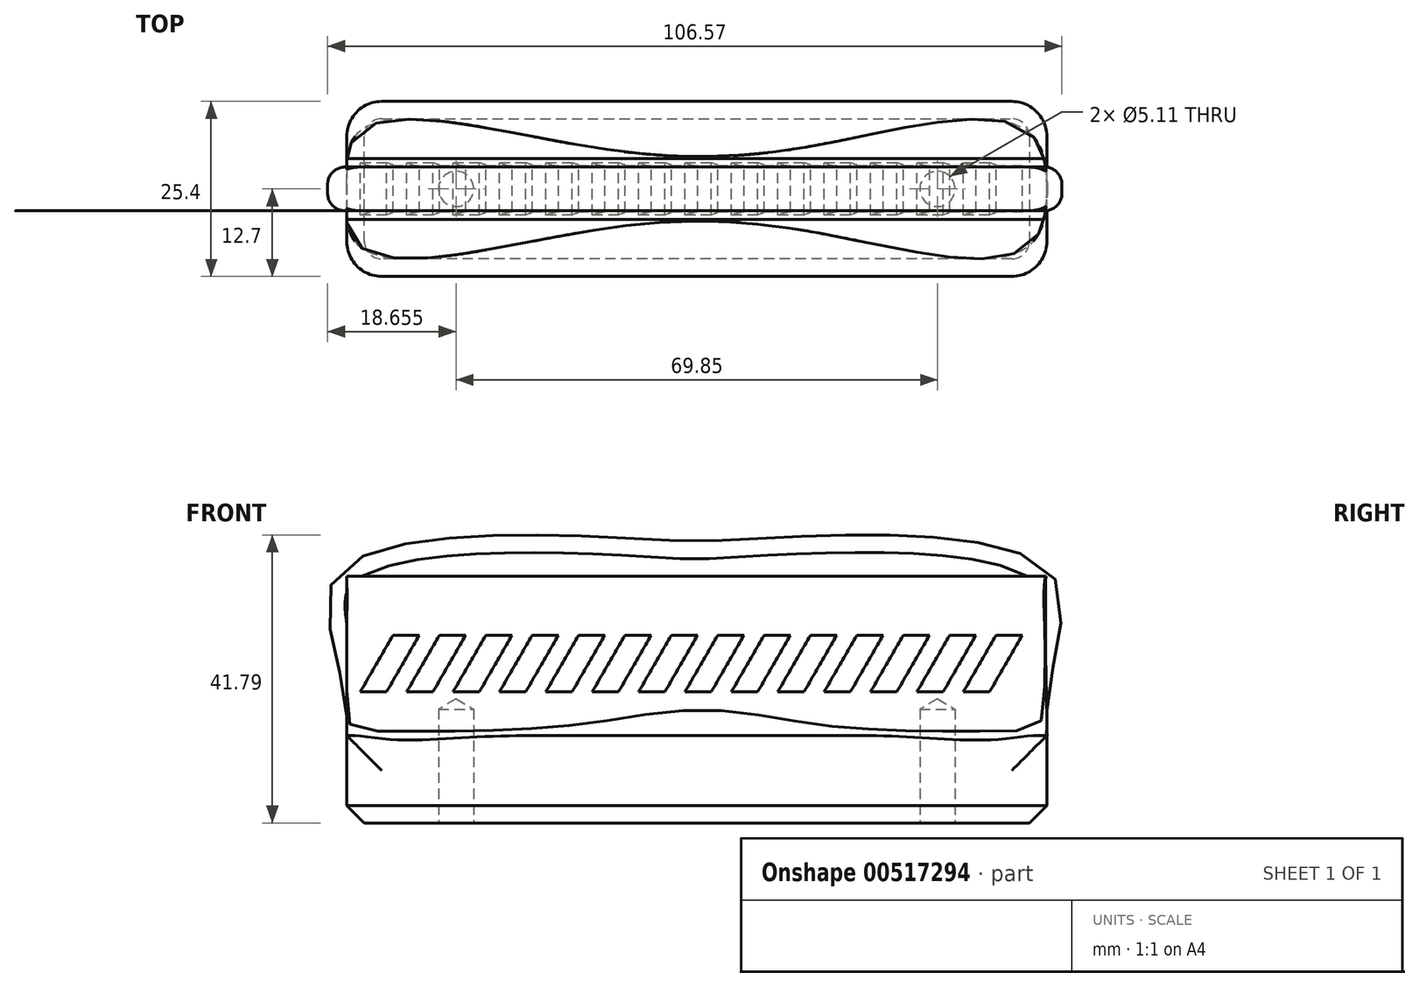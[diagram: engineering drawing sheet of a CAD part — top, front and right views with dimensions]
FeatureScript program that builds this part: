
annotation { "Feature Type Name" : "Feature", "Feature Type Description" : "" }
export const myFeature = defineFeature(function(context is Context, id is Id, definition is map)
    precondition{}
    {
        {
            var Q0;
            Q0=qCreatedBy(makeId("Front.planeOp"),FACE);
            var sketch = newSketch(context, id + "F0", { "sketchPlane" : qUnion([Q0])});
            skLineSegment(sketch, "E0.bottom", {"start": v(50.8, 6.35) * mm, "end": v(-50.8, 6.35) * mm});
            skLineSegment(sketch, "E0.top", {"start": v(50.8, -6.35) * mm, "end": v(-50.8, -6.35) * mm});
            skLineSegment(sketch, "E0.left", {"start": v(50.8, 6.35) * mm, "end": v(50.8, -6.35) * mm});
            skLineSegment(sketch, "E0.right", {"start": v(-50.8, 6.35) * mm, "end": v(-50.8, -6.35) * mm});
            skPoint(sketch, "E0.middle", {"position": v(0, 0) * mm});
            skSolve(sketch);
        }
        {
            var Q0;
            Q0=makeQuery(id+"F0.imprint","IMPRINT",FACE,{"disambiguationData":[TD([[makeQuery(id+"F0.imprint","IMPRINT",EDGE,{"derivedFrom":sQuery(id+"F0.wireOp",EDGE,"E0.bottom")}),1.0]])]});
            extrude(context, id + "F1", {"entities" : qUnion([Q0]), "endBound" : BoundingType.SYMMETRIC, "depth" : 25.4 * mm, "offsetDistance" : 25.4 * mm});
        }
        {
            var Q0;
            Q0=qCreatedBy(makeId("Front.planeOp"),FACE);
            var sketch = newSketch(context, id + "F2", { "sketchPlane" : qUnion([Q0])});
            skFitSpline(sketch, "E1", {"points": [v(-50.78, 6.4) * mm, v(-51.66, 30.38) * mm, v(-5.27, 34.72) * mm, v(5.16, 34.72) * mm, v(50.96, 30.38) * mm, v(50.85, 6.4) * mm], "startDerivative": vector(8.85, 159.27) * mm, "endDerivative": vector(16.11, -153.94) * mm});
            skLineSegment(sketch, "E2", {"start": v(-50.78, 6.4) * mm, "end": v(50.85, 6.4) * mm});
            skSolve(sketch);
        }
        {
            var Q0;
            Q0=makeQuery(id+"F2.imprint","IMPRINT",FACE,{"disambiguationData":[TD([[makeQuery(id+"F2.imprint","IMPRINT",EDGE,{"derivedFrom":sQuery(id+"F2.wireOp",EDGE,"E1")}),-1.0]])]});
            extrude(context, id + "F3", {"entities" : qUnion([Q0]), "operationType" : NewBodyOperationType.ADD, "endBound" : BoundingType.SYMMETRIC, "depth" : 6.35 * mm, "offsetDistance" : 25.4 * mm});
        }
        {
            var Q0;
            Q0=makeQuery(id+"F1.opExtrude","CAP_EDGE",EDGE,{"disambiguationData":[OSD([sQuery(id+"F0.wireOp",EDGE,"E0.right")])],"isStart":false});
            var Q1;
            Q1=makeQuery(id+"F1.opExtrude","CAP_EDGE",EDGE,{"disambiguationData":[OSD([sQuery(id+"F0.wireOp",EDGE,"E0.right")])],"isStart":true});
            var Q2;
            Q2=makeQuery(id+"F1.opExtrude","CAP_EDGE",EDGE,{"disambiguationData":[OSD([sQuery(id+"F0.wireOp",EDGE,"E0.left")])],"isStart":false});
            var Q3;
            Q3=makeQuery(id+"F1.opExtrude","CAP_EDGE",EDGE,{"disambiguationData":[OSD([sQuery(id+"F0.wireOp",EDGE,"E0.left")])],"isStart":true});
            fillet(context, id + "F4", {"entities" : qUnion([Q0, Q1, Q2, Q3]), "radius" : 5.08 * mm, "tangentPropagation" : true, "allowEdgeOverflow" : false});
        }
        {
            var Q0;
            Q0=makeQuery(id+"F3.opExtrude","CAP_EDGE",EDGE,{"disambiguationData":[OSD([sQuery(id+"F2.wireOp",EDGE,"E1")])],"isStart":false});
            var Q1;
            Q1=makeQuery(id+"F3.opExtrude","CAP_EDGE",EDGE,{"disambiguationData":[OSD([sQuery(id+"F2.wireOp",EDGE,"E1")])],"isStart":true});
            fillet(context, id + "F5", {"entities" : qUnion([Q0, Q1]), "radius" : 2.54 * mm, "tangentPropagation" : true, "allowEdgeOverflow" : false});
        }
        {
            var Q0;
            Q0=makeQuery(id+"F1.opExtrude","SWEPT_FACE",FACE,{"disambiguationData":[OSD([sQuery(id+"F0.wireOp",EDGE,"E0.bottom")])]});
            var sketch = newSketch(context, id + "F6", { "sketchPlane" : qUnion([Q0])});
            skFitSpline(sketch, "E3", {"points": [v(-50.8, 0) * mm, v(-49.62, 7.62) * mm, v(-40.46, 10.1) * mm, v(-13.35, 5.76) * mm, v(13.15, 5.64) * mm, v(39.23, 10.11) * mm, v(48.82, 7.62) * mm, v(50.8, 0) * mm], "startDerivative": vector(-2.84, 86.4) * mm, "endDerivative": vector(1.28, -86.45) * mm});
            skFitSpline(sketch, "E4.MirrorCS", {"points": [v(-50.8, 0) * mm, v(-49.62, -7.62) * mm, v(-40.46, -10.1) * mm, v(-13.35, -5.76) * mm, v(13.15, -5.64) * mm, v(39.23, -10.11) * mm, v(48.82, -7.62) * mm, v(50.8, 0) * mm], "startDerivative": vector(-2.84, -86.4) * mm, "endDerivative": vector(1.28, 86.45) * mm});
            skSolve(sketch);
        }
        {
            var Q0;
            {var subQ1=sQuery(id+"F6.wireOp",EDGE,"E3");var subQ2=sQuery(id+"F0.wireOp",EDGE,"E0.bottom");var subQ4=makeQuery(id+"F1.opExtrude","SWEPT_EDGE",EDGE,{"disambiguationData":[OSD([subQ2,sQuery(id+"F0.wireOp",EDGE,"E0.right")])]});var subQ5=makeQuery(id+"F6.imprint","INTERSECT",VERTEX,{"derivedFrom":[subQ4,subQ1]});Q0=makeQuery(id+"F6.imprint","IMPRINT",FACE,{"disambiguationData":[TD([[makeQuery(id+"F6.imprint","IMPRINT",EDGE,{"disambiguationData":[TD([[subQ5,-1.0]])],"derivedFrom":subQ1}),-1.0]])]});}
            extrude(context, id + "F7", {"entities" : qUnion([Q0]), "operationType" : NewBodyOperationType.ADD, "depth" : 23.1 * mm, "offsetDistance" : 25.4 * mm});
        }
        {
            var Q0;
            {var subQ0=sQuery(id+"F0.wireOp",EDGE,"E0.right");Q0=makeQuery(id+"F7.boolean.opBoolean","MERGE",FACE,{"derivedFrom":[makeQuery(id+"F1.opExtrude","SWEPT_FACE",FACE,{"disambiguationData":[OSD([subQ0])]}),makeQuery(id+"F7.opExtrude","SWEPT_FACE",FACE,{"disambiguationData":[OSD([sQuery(id+"F0.wireOp",EDGE,"E0.bottom"),subQ0])]})]});}
            var sketch = newSketch(context, id + "F8", { "sketchPlane" : qUnion([Q0])});
            skFitSpline(sketch, "E5", {"points": [v(-5.34, 32.34) * mm, v(-3.75, 23.34) * mm, v(-5.9, 8.32) * mm, v(-14.33, 6.78) * mm], "startDerivative": vector(-7.09, -60.22) * mm, "endDerivative": vector(-24.18, -5.78) * mm});
            skLineSegment(sketch, "E6", {"start": v(-14.33, 6.78) * mm, "end": v(-14.33, 32.34) * mm});
            skLineSegment(sketch, "E7", {"start": v(-14.33, 32.34) * mm, "end": v(-5.34, 32.34) * mm});
            skLineSegment(sketch, "E8.MirrorCS", {"start": v(14.33, 6.78) * mm, "end": v(14.33, 32.34) * mm});
            skLineSegment(sketch, "E9.MirrorCS", {"start": v(14.33, 32.34) * mm, "end": v(5.34, 32.34) * mm});
            skFitSpline(sketch, "E10.MirrorCS", {"points": [v(5.34, 32.34) * mm, v(3.75, 23.34) * mm, v(5.9, 8.32) * mm, v(14.33, 6.78) * mm], "startDerivative": vector(7.09, -60.22) * mm, "endDerivative": vector(24.18, -5.78) * mm});
            skSolve(sketch);
        }
        {
            var Q0;
            Q0 = qSketchRegion(id + "F8", true);
            extrude(context, id + "F9", {"entities" : qUnion([Q0]), "operationType" : NewBodyOperationType.REMOVE, "endBound" : BoundingType.THROUGH_ALL, "oppositeDirection" : true, "depth" : 109.22 * mm, "offsetDistance" : 25.4 * mm, "hasSecondDirection" : true, "secondDirectionBound" : SecondDirectionBoundingType.THROUGH_ALL, "secondDirectionOppositeDirection" : false, "secondDirectionDepth" : 25.4 * mm});
        }
        {
            var Q0;
            Q0=makeQuery(id+"F9.boolean.opBoolean","INTERSECT",EDGE,{"disambiguationData":[OD(1.0)],"derivedFrom":[makeQuery(id+"F7.opExtrude","CAP_FACE",FACE,{"disambiguationData":[OSD([sQuery(id+"F0.wireOp",EDGE,"E0.bottom"),sQuery(id+"F0.wireOp",EDGE,"E0.right"),sQuery(id+"F6.wireOp",EDGE,"E3"),sQuery(id+"F6.wireOp",EDGE,"E4.MirrorCS")])],"isStart":false}),makeQuery(id+"F9.opExtrude","SWEPT_FACE",FACE,{"disambiguationData":[OSD([sQuery(id+"F8.wireOp",EDGE,"E10.MirrorCS")])]})]});
            var Q1;
            Q1=makeQuery(id+"F9.boolean.opBoolean","INTERSECT",EDGE,{"disambiguationData":[OD(1.0)],"derivedFrom":[makeQuery(id+"F7.opExtrude","CAP_FACE",FACE,{"disambiguationData":[OSD([sQuery(id+"F0.wireOp",EDGE,"E0.bottom"),sQuery(id+"F0.wireOp",EDGE,"E0.right"),sQuery(id+"F6.wireOp",EDGE,"E3"),sQuery(id+"F6.wireOp",EDGE,"E4.MirrorCS")])],"isStart":false}),makeQuery(id+"F9.opExtrude","SWEPT_FACE",FACE,{"disambiguationData":[OSD([sQuery(id+"F8.wireOp",EDGE,"E5")])]})]});
            fillet(context, id + "F10", {"entities" : qUnion([Q0, Q1]), "radius" : 5.08 * mm, "tangentPropagation" : true, "allowEdgeOverflow" : false});
        }
        {
            var Q0;
            Q0=makeQuery(id+"F1.opExtrude","SWEPT_FACE",FACE,{"disambiguationData":[OSD([sQuery(id+"F0.wireOp",EDGE,"E0.top")])]});
            var sketch = newSketch(context, id + "F11", { "sketchPlane" : qUnion([Q0])});
            skPoint(sketch, "E11", {"position": v(-34.93, 0) * mm});
            skPoint(sketch, "E12", {"position": v(34.93, 0) * mm});
            skSolve(sketch);
        }
        {
            var Q0;
            Q0=sQuery(id+"F11.wireOp",VERTEX,"E11");
            var Q1;
            Q1=sQuery(id+"F11.wireOp",VERTEX,"E12");
            var Q2;
            Q2=makeQuery(id+"F1.opExtrude","SWEPT_BODY",BODY,{"disambiguationData":[OSD([sQuery(id+"F0.wireOp",EDGE,"E0.bottom"),sQuery(id+"F0.wireOp",EDGE,"E0.top"),sQuery(id+"F0.wireOp",EDGE,"E0.left"),sQuery(id+"F0.wireOp",EDGE,"E0.right")])]});
            hole(context, id + "F12", {"style" : HoleStyle.SIMPLE, "endStyle" : HoleEndStyle.BLIND, "standardTappedOrClearance" : lookupTablePath({ "standard" : "ANSI", "engagement" : "75%", "pitch" : "20 tpi", "size" : "1/4", "type" : "Tapped" }), "standardBlindInLast" : lookupTablePath({ "standard" : "ANSI", "engagement" : "75%", "pitch" : "20 tpi", "size" : "1/4", "type" : "Tapped" }), "holeDiameter" : 5.1 * mm, "showTappedDepth" : true, "holeDepth" : 16.51 * mm, "isTappedThrough" : true, "tappedDepth" : 12.7 * mm, "tapClearance" : 3, "locations" : qUnion([Q0, Q1]), "scope" : qUnion([Q2]), "majorDiameter" : 6.35 * mm});
        }
        {
            var Q0;
            Q0=qCreatedBy(makeId("Front.planeOp"),FACE);
            var sketch = newSketch(context, id + "F13", { "sketchPlane" : qUnion([Q0])});
            skLineSegment(sketch, "E13", {"start": v(-48.82, 12.7) * mm, "end": v(-44.09, 20.9) * mm});
            skLineSegment(sketch, "E14", {"start": v(-44.09, 20.9) * mm, "end": v(-40.28, 20.9) * mm});
            skLineSegment(sketch, "E15", {"start": v(-40.28, 20.9) * mm, "end": v(-45, 12.7) * mm});
            skLineSegment(sketch, "E16", {"start": v(-45, 12.7) * mm, "end": v(-48.82, 12.7) * mm});
            skLineSegment(sketch, "E17.1.0.0", {"start": v(-42.09, 12.7) * mm, "end": v(-37.36, 20.9) * mm});
            skLineSegment(sketch, "E17.1.0.1", {"start": v(-37.36, 20.9) * mm, "end": v(-33.55, 20.9) * mm});
            skLineSegment(sketch, "E17.1.0.2", {"start": v(-38.28, 12.7) * mm, "end": v(-42.09, 12.7) * mm});
            skLineSegment(sketch, "E17.1.0.3", {"start": v(-33.55, 20.9) * mm, "end": v(-38.28, 12.7) * mm});
            skLineSegment(sketch, "E17.2.0.0", {"start": v(-35.35, 12.7) * mm, "end": v(-30.63, 20.9) * mm});
            skLineSegment(sketch, "E17.2.0.1", {"start": v(-30.63, 20.9) * mm, "end": v(-26.82, 20.9) * mm});
            skLineSegment(sketch, "E17.2.0.2", {"start": v(-31.54, 12.7) * mm, "end": v(-35.35, 12.7) * mm});
            skLineSegment(sketch, "E17.2.0.3", {"start": v(-26.82, 20.9) * mm, "end": v(-31.54, 12.7) * mm});
            skLineSegment(sketch, "E17.3.0.0", {"start": v(-28.62, 12.7) * mm, "end": v(-23.9, 20.9) * mm});
            skLineSegment(sketch, "E17.3.0.1", {"start": v(-23.9, 20.9) * mm, "end": v(-20.08, 20.9) * mm});
            skLineSegment(sketch, "E17.3.0.2", {"start": v(-24.81, 12.7) * mm, "end": v(-28.62, 12.7) * mm});
            skLineSegment(sketch, "E17.3.0.3", {"start": v(-20.08, 20.9) * mm, "end": v(-24.81, 12.7) * mm});
            skLineSegment(sketch, "E17.4.0.0", {"start": v(-21.9, 12.7) * mm, "end": v(-17.16, 20.9) * mm});
            skLineSegment(sketch, "E17.4.0.1", {"start": v(-17.16, 20.9) * mm, "end": v(-13.35, 20.9) * mm});
            skLineSegment(sketch, "E17.4.0.2", {"start": v(-18.08, 12.7) * mm, "end": v(-21.9, 12.7) * mm});
            skLineSegment(sketch, "E17.4.0.3", {"start": v(-13.35, 20.9) * mm, "end": v(-18.08, 12.7) * mm});
            skLineSegment(sketch, "E17.5.0.0", {"start": v(-15.16, 12.7) * mm, "end": v(-10.43, 20.9) * mm});
            skLineSegment(sketch, "E17.5.0.1", {"start": v(-10.43, 20.9) * mm, "end": v(-6.62, 20.9) * mm});
            skLineSegment(sketch, "E17.5.0.2", {"start": v(-11.35, 12.7) * mm, "end": v(-15.16, 12.7) * mm});
            skLineSegment(sketch, "E17.5.0.3", {"start": v(-6.62, 20.9) * mm, "end": v(-11.35, 12.7) * mm});
            skLineSegment(sketch, "E17.6.0.0", {"start": v(-8.43, 12.7) * mm, "end": v(-3.7, 20.9) * mm});
            skLineSegment(sketch, "E17.6.0.1", {"start": v(-3.7, 20.9) * mm, "end": v(0.1, 20.9) * mm});
            skLineSegment(sketch, "E17.6.0.2", {"start": v(-4.62, 12.7) * mm, "end": v(-8.43, 12.7) * mm});
            skLineSegment(sketch, "E17.6.0.3", {"start": v(0.1, 20.9) * mm, "end": v(-4.62, 12.7) * mm});
            skLineSegment(sketch, "E17.direction1", {"start": v(-48.82, 12.7) * mm, "end": v(-42.09, 12.7) * mm, "construction": true});
            skLineSegment(sketch, "E18.0.7.0", {"start": v(-1.7, 12.7) * mm, "end": v(3.03, 20.9) * mm});
            skLineSegment(sketch, "E18.3.7.0", {"start": v(3.03, 20.9) * mm, "end": v(6.84, 20.9) * mm});
            skLineSegment(sketch, "E18.6.7.0", {"start": v(2.11, 12.7) * mm, "end": v(-1.7, 12.7) * mm});
            skLineSegment(sketch, "E18.9.7.0", {"start": v(6.84, 20.9) * mm, "end": v(2.11, 12.7) * mm});
            skLineSegment(sketch, "E18.0.8.0", {"start": v(5.03, 12.7) * mm, "end": v(9.76, 20.9) * mm});
            skLineSegment(sketch, "E18.3.8.0", {"start": v(9.76, 20.9) * mm, "end": v(13.57, 20.9) * mm});
            skLineSegment(sketch, "E18.6.8.0", {"start": v(8.84, 12.7) * mm, "end": v(5.03, 12.7) * mm});
            skLineSegment(sketch, "E18.9.8.0", {"start": v(13.57, 20.9) * mm, "end": v(8.84, 12.7) * mm});
            skLineSegment(sketch, "E18.0.9.0", {"start": v(11.76, 12.7) * mm, "end": v(16.5, 20.9) * mm});
            skLineSegment(sketch, "E18.3.9.0", {"start": v(16.5, 20.9) * mm, "end": v(20.3, 20.9) * mm});
            skLineSegment(sketch, "E18.6.9.0", {"start": v(15.57, 12.7) * mm, "end": v(11.76, 12.7) * mm});
            skLineSegment(sketch, "E18.9.9.0", {"start": v(20.3, 20.9) * mm, "end": v(15.57, 12.7) * mm});
            skLineSegment(sketch, "E18.0.10.0", {"start": v(18.5, 12.7) * mm, "end": v(23.22, 20.9) * mm});
            skLineSegment(sketch, "E18.3.10.0", {"start": v(23.22, 20.9) * mm, "end": v(27.03, 20.9) * mm});
            skLineSegment(sketch, "E18.6.10.0", {"start": v(22.3, 12.7) * mm, "end": v(18.5, 12.7) * mm});
            skLineSegment(sketch, "E18.9.10.0", {"start": v(27.03, 20.9) * mm, "end": v(22.3, 12.7) * mm});
            skLineSegment(sketch, "E18.0.11.0", {"start": v(25.22, 12.7) * mm, "end": v(29.95, 20.9) * mm});
            skLineSegment(sketch, "E18.3.11.0", {"start": v(29.95, 20.9) * mm, "end": v(33.76, 20.9) * mm});
            skLineSegment(sketch, "E18.6.11.0", {"start": v(29.03, 12.7) * mm, "end": v(25.22, 12.7) * mm});
            skLineSegment(sketch, "E18.9.11.0", {"start": v(33.76, 20.9) * mm, "end": v(29.03, 12.7) * mm});
            skLineSegment(sketch, "E18.0.12.0", {"start": v(31.96, 12.7) * mm, "end": v(36.68, 20.9) * mm});
            skLineSegment(sketch, "E18.3.12.0", {"start": v(36.68, 20.9) * mm, "end": v(40.5, 20.9) * mm});
            skLineSegment(sketch, "E18.6.12.0", {"start": v(35.77, 12.7) * mm, "end": v(31.96, 12.7) * mm});
            skLineSegment(sketch, "E18.9.12.0", {"start": v(40.5, 20.9) * mm, "end": v(35.77, 12.7) * mm});
            skLineSegment(sketch, "E18.0.13.0", {"start": v(38.69, 12.7) * mm, "end": v(43.42, 20.9) * mm});
            skLineSegment(sketch, "E18.3.13.0", {"start": v(43.42, 20.9) * mm, "end": v(47.23, 20.9) * mm});
            skLineSegment(sketch, "E18.6.13.0", {"start": v(42.5, 12.7) * mm, "end": v(38.69, 12.7) * mm});
            skLineSegment(sketch, "E18.9.13.0", {"start": v(47.23, 20.9) * mm, "end": v(42.5, 12.7) * mm});
            skSolve(sketch);
        }
        {
            var Q0;
            Q0 = qSketchRegion(id + "F13", true);
            extrude(context, id + "F14", {"entities" : qUnion([Q0]), "operationType" : NewBodyOperationType.REMOVE, "endBound" : BoundingType.THROUGH_ALL, "depth" : 25.4 * mm, "offsetDistance" : 25.4 * mm, "hasSecondDirection" : true, "secondDirectionBound" : SecondDirectionBoundingType.THROUGH_ALL, "secondDirectionOppositeDirection" : true, "secondDirectionDepth" : 25.4 * mm});
        }
        {
            var Q0;
            Q0=makeQuery(id+"F1.opExtrude","CAP_EDGE",EDGE,{"disambiguationData":[OSD([sQuery(id+"F0.wireOp",EDGE,"E0.bottom")])],"isStart":false});
            var Q1;
            Q1=makeQuery(id+"F1.opExtrude","CAP_EDGE",EDGE,{"disambiguationData":[OSD([sQuery(id+"F0.wireOp",EDGE,"E0.bottom")])],"isStart":true});
            fillet(context, id + "F15", {"entities" : qUnion([Q0, Q1]), "radius" : 5.08 * mm, "allowEdgeOverflow" : false});
        }
        {
            var Q0;
            Q0=makeQuery(id+"F1.opExtrude","CAP_EDGE",EDGE,{"disambiguationData":[OSD([sQuery(id+"F0.wireOp",EDGE,"E0.top")])],"isStart":false});
            chamfer(context, id + "F16", {"entities" : qUnion([Q0]), "width" : 2.54 * mm, "tangentPropagation" : true});
        }
    });
